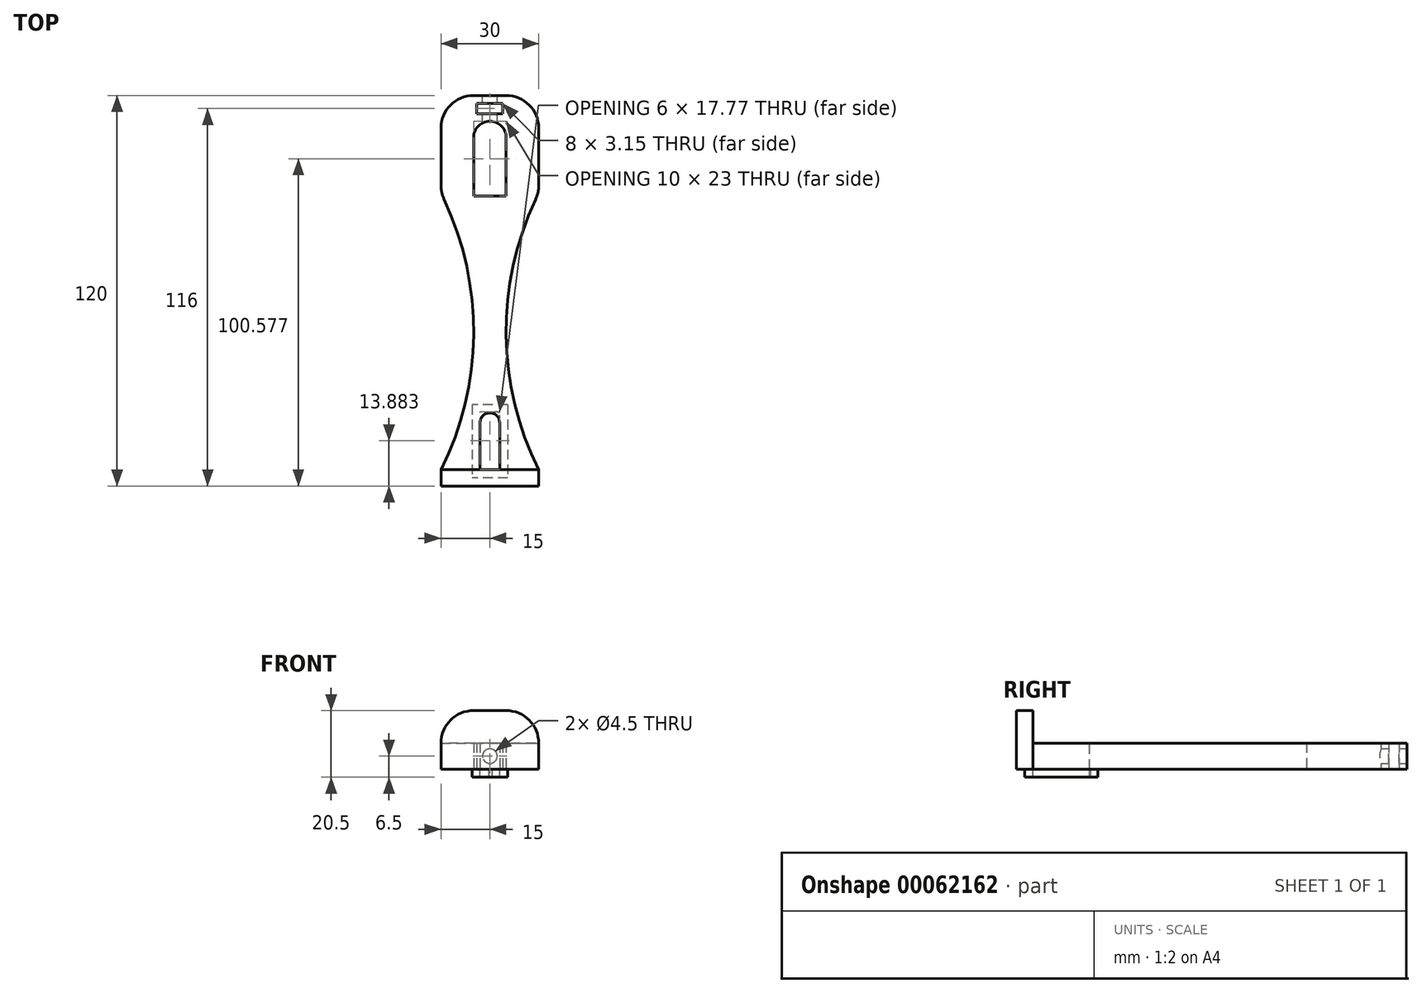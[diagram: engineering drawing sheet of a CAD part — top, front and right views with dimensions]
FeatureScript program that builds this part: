
annotation { "Feature Type Name" : "Feature", "Feature Type Description" : "" }
export const myFeature = defineFeature(function(context is Context, id is Id, definition is map)
    precondition{}
    {
        {
            var Q0;
            Q0=qCreatedBy(makeId("Top.planeOp"),FACE);
            var sketch = newSketch(context, id + "F0", { "sketchPlane" : qUnion([Q0])});
            skLineSegment(sketch, "E0.bottom", {"start": v(-15, 0) * mm, "end": v(15, 0) * mm});
            skLineSegment(sketch, "E0.top", {"start": v(-15, 115) * mm, "end": v(15, 115) * mm});
            skLineSegment(sketch, "E0.left", {"start": v(-15, 85) * mm, "end": v(-15, 115) * mm});
            skLineSegment(sketch, "E0.right", {"start": v(15, 85) * mm, "end": v(15, 115) * mm});
            skPoint(sketch, "E1", {"position": v(-15, 85) * mm});
            skPoint(sketch, "E2", {"position": v(15, 85) * mm});
            skArc(sketch, "E3", {"start": v(-15, 0) * mm, "mid": v(-5, 42.5) * mm, "end": v(-15, 85) * mm});
            skArc(sketch, "E4", {"start": v(15, 85) * mm, "mid": v(5, 42.5) * mm, "end": v(15, 0) * mm});
            skLineSegment(sketch, "E5.rect.bottom", {"start": v(4, 109.43) * mm, "end": v(-4, 109.43) * mm});
            skLineSegment(sketch, "E5.rect.top", {"start": v(4, 112.58) * mm, "end": v(-4, 112.58) * mm});
            skLineSegment(sketch, "E5.rect.left", {"start": v(4, 109.43) * mm, "end": v(4, 112.58) * mm});
            skLineSegment(sketch, "E5.rect.right", {"start": v(-4, 109.43) * mm, "end": v(-4, 112.58) * mm});
            skPoint(sketch, "E5.rect.middle", {"position": v(0, 111) * mm});
            skLineSegment(sketch, "E6.rect.bottom", {"start": v(5, 107.08) * mm, "end": v(-5, 107.08) * mm});
            skLineSegment(sketch, "E6.rect.top", {"start": v(5, 84.08) * mm, "end": v(-5, 84.08) * mm});
            skLineSegment(sketch, "E6.rect.left", {"start": v(5, 107.08) * mm, "end": v(5, 84.08) * mm});
            skLineSegment(sketch, "E6.rect.right", {"start": v(-5, 107.08) * mm, "end": v(-5, 84.08) * mm});
            skPoint(sketch, "E6.rect.middle", {"position": v(0, 95.58) * mm});
            skLineSegment(sketch, "E7", {"start": v(-15, 85) * mm, "end": v(15, 85) * mm, "construction": true});
            skLineSegment(sketch, "E8.bottom", {"start": v(-2.7, 0) * mm, "end": v(2.3, 0) * mm});
            skSolve(sketch);
        }
        {
            var Q0;
            Q0 = qSketchRegion(id + "F0", true);
            extrude(context, id + "F1", {"entities" : qUnion([Q0]), "depth" : 8 * mm});
        }
        {
            var Q0;
            Q0=makeQuery(id+"F1.opExtrude","SWEPT_FACE",FACE,{"disambiguationData":[OSD([sQuery(id+"F0.wireOp",EDGE,"E0.bottom")])]});
            var sketch = newSketch(context, id + "F2", { "sketchPlane" : qUnion([Q0])});
            skLineSegment(sketch, "E9.bottom", {"start": v(-15, 0) * mm, "end": v(15, 0) * mm});
            skLineSegment(sketch, "E9.top", {"start": v(-15, 18) * mm, "end": v(15, 18) * mm});
            skLineSegment(sketch, "E9.left", {"start": v(-15, 0) * mm, "end": v(-15, 18) * mm});
            skLineSegment(sketch, "E9.right", {"start": v(15, 0) * mm, "end": v(15, 18) * mm});
            skSolve(sketch);
        }
        {
            var Q0;
            Q0 = qSketchRegion(id + "F2", true);
            extrude(context, id + "F3", {"entities" : qUnion([Q0]), "operationType" : NewBodyOperationType.ADD, "depth" : 5 * mm});
        }
        {
            var Q0;
            Q0=makeQuery(id+"F1.opExtrude","SWEPT_FACE",FACE,{"disambiguationData":[OSD([sQuery(id+"F0.wireOp",EDGE,"E0.top")])]});
            var sketch = newSketch(context, id + "F4", { "sketchPlane" : qUnion([Q0])});
            skCircle(sketch, "E10", {"center": v(0, 4) * mm, "radius": 2.25 * mm});
            skPoint(sketch, "E10.centerSnap0", {"position": v(0, 0) * mm});
            skLineSegment(sketch, "E11", {"start": v(0, 0) * mm, "end": v(0, 8) * mm, "construction": true});
            skSolve(sketch);
        }
        {
            var Q0;
            Q0 = qSketchRegion(id + "F4", true);
            extrude(context, id + "F5", {"entities" : qUnion([Q0]), "operationType" : NewBodyOperationType.REMOVE, "oppositeDirection" : true, "depth" : 10 * mm});
        }
        {
            var Q0;
            Q0=makeQuery(id+"F3.boolean.opBoolean","MERGE",FACE,{"derivedFrom":[makeQuery(id+"F1.opExtrude","CAP_FACE",FACE,{"disambiguationData":[OSD([sQuery(id+"F0.wireOp",EDGE,"E0.bottom"),sQuery(id+"F0.wireOp",EDGE,"E0.top"),sQuery(id+"F0.wireOp",EDGE,"E0.left"),sQuery(id+"F0.wireOp",EDGE,"E0.right"),sQuery(id+"F0.wireOp",EDGE,"E3"),sQuery(id+"F0.wireOp",EDGE,"E4"),sQuery(id+"F0.wireOp",EDGE,"E5.rect.bottom"),sQuery(id+"F0.wireOp",EDGE,"E5.rect.top"),sQuery(id+"F0.wireOp",EDGE,"E5.rect.left"),sQuery(id+"F0.wireOp",EDGE,"E5.rect.right"),sQuery(id+"F0.wireOp",EDGE,"E6.rect.bottom"),sQuery(id+"F0.wireOp",EDGE,"E6.rect.top"),sQuery(id+"F0.wireOp",EDGE,"E6.rect.left"),sQuery(id+"F0.wireOp",EDGE,"E6.rect.right"),sQuery(id+"F0.wireOp",EDGE,"E8.bottom")])],"isStart":true}),makeQuery(id+"F3.opExtrude","SWEPT_FACE",FACE,{"disambiguationData":[OSD([sQuery(id+"F2.wireOp",EDGE,"E9.bottom")])]})]});
            var sketch = newSketch(context, id + "F6", { "sketchPlane" : qUnion([Q0])});
            skLineSegment(sketch, "E12.bottom", {"start": v(-3, 0) * mm, "end": v(3, 0) * mm});
            skLineSegment(sketch, "E12.top", {"start": v(-3, -17.5) * mm, "end": v(3, -17.5) * mm});
            skLineSegment(sketch, "E12.left", {"start": v(-3, 0) * mm, "end": v(-3, -17.5) * mm});
            skLineSegment(sketch, "E12.right", {"start": v(3, 0) * mm, "end": v(3, -17.5) * mm});
            skSolve(sketch);
        }
        {
            var Q0;
            Q0 = qSketchRegion(id + "F6", true);
            extrude(context, id + "F7", {"entities" : qUnion([Q0]), "operationType" : NewBodyOperationType.REMOVE, "oppositeDirection" : true, "depth" : 25 * mm});
        }
        {
            var Q0;
            Q0=makeQuery(id+"F1.opExtrude","SWEPT_EDGE",EDGE,{"disambiguationData":[OSD([sQuery(id+"F0.wireOp",EDGE,"E0.top"),sQuery(id+"F0.wireOp",EDGE,"E0.right")])]});
            var Q1;
            Q1=makeQuery(id+"F1.opExtrude","SWEPT_EDGE",EDGE,{"disambiguationData":[OSD([sQuery(id+"F0.wireOp",EDGE,"E0.top"),sQuery(id+"F0.wireOp",EDGE,"E0.left")])]});
            fillet(context, id + "F8", {"entities" : qUnion([Q0, Q1]), "radius" : 10 * mm, "tangentPropagation" : true, "allowEdgeOverflow" : false});
        }
        {
            var Q0;
            Q0=makeQuery(id+"F1.opExtrude","SWEPT_EDGE",EDGE,{"disambiguationData":[OSD([sQuery(id+"F0.wireOp",EDGE,"E0.right"),sQuery(id+"F0.wireOp",EDGE,"E4")])]});
            var Q1;
            Q1=makeQuery(id+"F1.opExtrude","SWEPT_EDGE",EDGE,{"disambiguationData":[OSD([sQuery(id+"F0.wireOp",EDGE,"E0.left"),sQuery(id+"F0.wireOp",EDGE,"E3")])]});
            fillet(context, id + "F9", {"entities" : qUnion([Q0, Q1]), "radius" : 10 * mm, "tangentPropagation" : true, "allowEdgeOverflow" : false});
        }
        {
            var Q0;
            Q0=makeQuery(id+"F1.opExtrude","SWEPT_EDGE",EDGE,{"disambiguationData":[OSD([sQuery(id+"F0.wireOp",EDGE,"E6.rect.bottom"),sQuery(id+"F0.wireOp",EDGE,"E6.rect.right")])]});
            var Q1;
            Q1=makeQuery(id+"F1.opExtrude","SWEPT_EDGE",EDGE,{"disambiguationData":[OSD([sQuery(id+"F0.wireOp",EDGE,"E6.rect.bottom"),sQuery(id+"F0.wireOp",EDGE,"E6.rect.left")])]});
            fillet(context, id + "F10", {"entities" : qUnion([Q0, Q1]), "radius" : 5 * mm, "tangentPropagation" : true, "allowEdgeOverflow" : false});
        }
        {
            var Q0;
            Q0=makeQuery(id+"F7.boolean.opBoolean","COPY",EDGE,{"derivedFrom":makeQuery(id+"F7.opExtrude","SWEPT_EDGE",EDGE,{"disambiguationData":[OSD([sQuery(id+"F6.wireOp",EDGE,"E12.top"),sQuery(id+"F6.wireOp",EDGE,"E12.left")])]})});
            var Q1;
            Q1=makeQuery(id+"F7.boolean.opBoolean","COPY",EDGE,{"derivedFrom":makeQuery(id+"F7.opExtrude","SWEPT_EDGE",EDGE,{"disambiguationData":[OSD([sQuery(id+"F6.wireOp",EDGE,"E12.top"),sQuery(id+"F6.wireOp",EDGE,"E12.right")])]})});
            fillet(context, id + "F11", {"entities" : qUnion([Q0, Q1]), "radius" : 3 * mm, "tangentPropagation" : true, "allowEdgeOverflow" : false});
        }
        {
            var Q0;
            Q0=makeQuery(id+"F3.opExtrude","SWEPT_EDGE",EDGE,{"disambiguationData":[OSD([sQuery(id+"F2.wireOp",EDGE,"E9.top"),sQuery(id+"F2.wireOp",EDGE,"E9.right")])]});
            var Q1;
            Q1=makeQuery(id+"F3.opExtrude","SWEPT_EDGE",EDGE,{"disambiguationData":[OSD([sQuery(id+"F2.wireOp",EDGE,"E9.top"),sQuery(id+"F2.wireOp",EDGE,"E9.left")])]});
            fillet(context, id + "F12", {"entities" : qUnion([Q0, Q1]), "radius" : 10 * mm, "tangentPropagation" : true, "allowEdgeOverflow" : false});
        }
        {
            var Q0;
            Q0=makeQuery(id+"F3.boolean.opBoolean","MERGE",FACE,{"derivedFrom":[makeQuery(id+"F1.opExtrude","CAP_FACE",FACE,{"disambiguationData":[OSD([sQuery(id+"F0.wireOp",EDGE,"E0.bottom"),sQuery(id+"F0.wireOp",EDGE,"E0.top"),sQuery(id+"F0.wireOp",EDGE,"E0.left"),sQuery(id+"F0.wireOp",EDGE,"E0.right"),sQuery(id+"F0.wireOp",EDGE,"E3"),sQuery(id+"F0.wireOp",EDGE,"E4"),sQuery(id+"F0.wireOp",EDGE,"E5.rect.bottom"),sQuery(id+"F0.wireOp",EDGE,"E5.rect.top"),sQuery(id+"F0.wireOp",EDGE,"E5.rect.left"),sQuery(id+"F0.wireOp",EDGE,"E5.rect.right"),sQuery(id+"F0.wireOp",EDGE,"E6.rect.bottom"),sQuery(id+"F0.wireOp",EDGE,"E6.rect.top"),sQuery(id+"F0.wireOp",EDGE,"E6.rect.left"),sQuery(id+"F0.wireOp",EDGE,"E6.rect.right"),sQuery(id+"F0.wireOp",EDGE,"E8.bottom")])],"isStart":true}),makeQuery(id+"F3.opExtrude","SWEPT_FACE",FACE,{"disambiguationData":[OSD([sQuery(id+"F2.wireOp",EDGE,"E9.bottom")])]})]});
            var sketch = newSketch(context, id + "F13", { "sketchPlane" : qUnion([Q0])});
            skArc(sketch, "E13.0", {"start": v(3, -17.5) * mm, "mid": v(1.86, -17.77) * mm, "end": v(0.73, -17.49) * mm});
            skLineSegment(sketch, "E13.1", {"start": v(-0.27, -17.49) * mm, "end": v(0.73, -17.49) * mm});
            skArc(sketch, "E13.2", {"start": v(-0.27, -17.49) * mm, "mid": v(-2.22, -16.52) * mm, "end": v(-3, -14.5) * mm});
            skLineSegment(sketch, "E13.3", {"start": v(-3, 0) * mm, "end": v(-3, -14.5) * mm});
            skLineSegment(sketch, "E13.4", {"start": v(-3, 0) * mm, "end": v(3, 0) * mm});
            skLineSegment(sketch, "E13.5", {"start": v(3, 0) * mm, "end": v(3, -17.5) * mm});
            skLineSegment(sketch, "E14.bottom", {"start": v(5.5, -19.99) * mm, "end": v(-5.5, -19.99) * mm});
            skLineSegment(sketch, "E14.top", {"start": v(5.5, 2.5) * mm, "end": v(-5.5, 2.5) * mm});
            skLineSegment(sketch, "E14.left", {"start": v(5.5, -19.99) * mm, "end": v(5.5, 2.5) * mm});
            skLineSegment(sketch, "E14.right", {"start": v(-5.5, -19.99) * mm, "end": v(-5.5, 2.5) * mm});
            skSolve(sketch);
        }
        {
            var Q0;
            Q0 = qSketchRegion(id + "F13", true);
            extrude(context, id + "F14", {"entities" : qUnion([Q0]), "depth" : 2.5 * mm});
        }
    });
